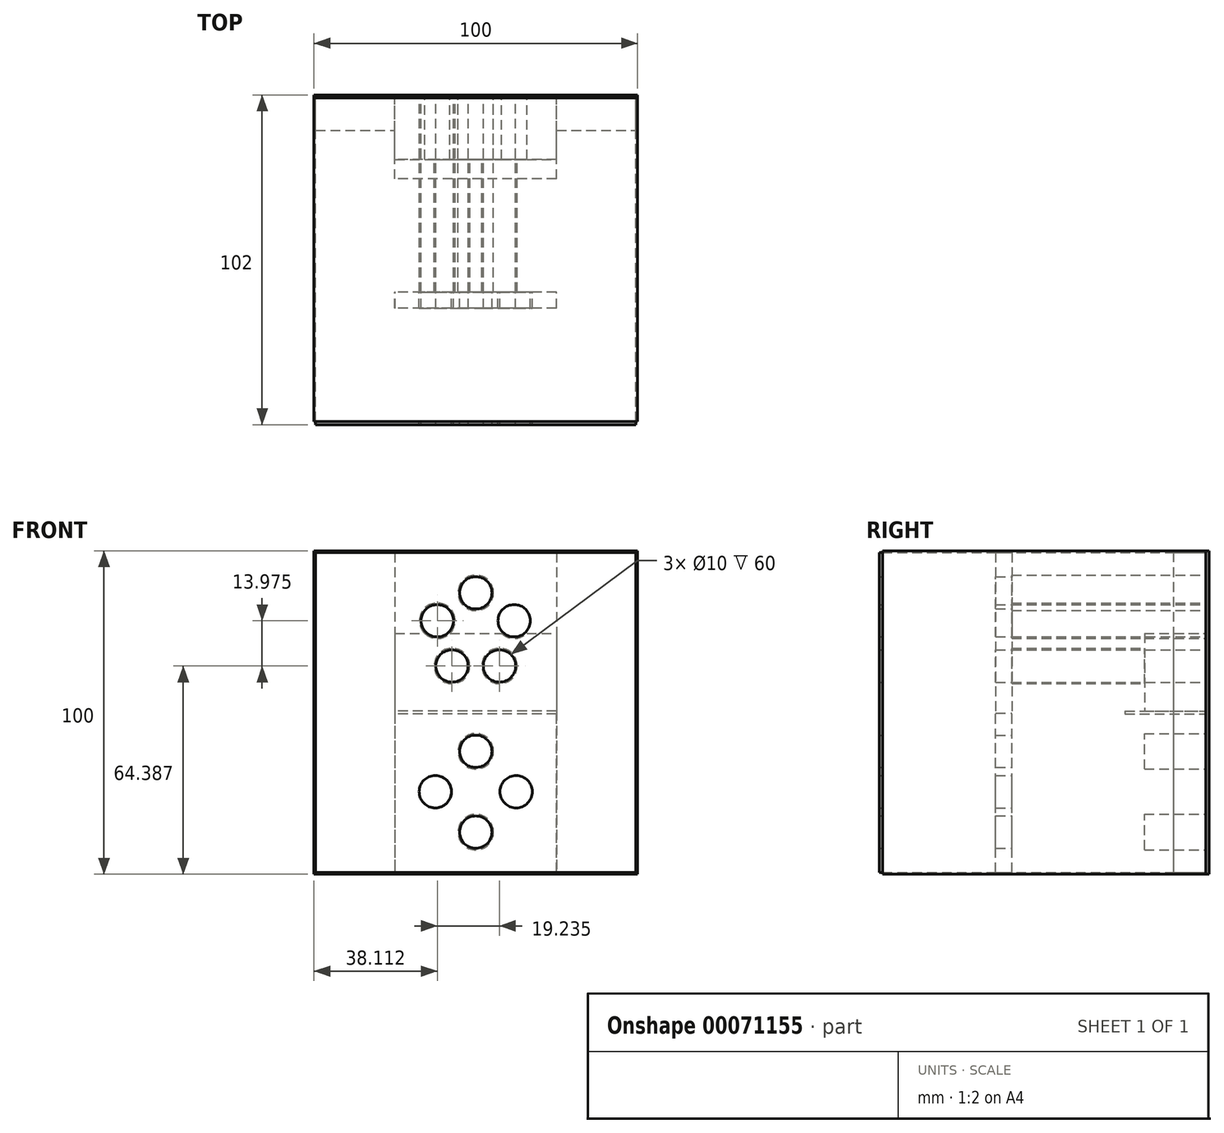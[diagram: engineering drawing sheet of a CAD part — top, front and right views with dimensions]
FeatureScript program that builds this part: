
annotation { "Feature Type Name" : "Feature", "Feature Type Description" : "" }
export const myFeature = defineFeature(function(context is Context, id is Id, definition is map)
    precondition{}
    {
        {
            var Q0;
            Q0=qCreatedBy(makeId("Front.planeOp"),FACE);
            var sketch = newSketch(context, id + "F0", { "sketchPlane" : qUnion([Q0])});
            skLineSegment(sketch, "E0.rect.bottom", {"start": v(-49.5, 49.5) * mm, "end": v(49.5, 49.5) * mm});
            skLineSegment(sketch, "E0.rect.top", {"start": v(-49.5, -49.5) * mm, "end": v(49.5, -49.5) * mm});
            skLineSegment(sketch, "E0.rect.left", {"start": v(-49.5, 49.5) * mm, "end": v(-49.5, -49.5) * mm});
            skLineSegment(sketch, "E0.rect.right", {"start": v(49.5, 49.5) * mm, "end": v(49.5, -49.5) * mm});
            skPoint(sketch, "E0.rect.middle", {"position": v(0, 0) * mm});
            skLineSegment(sketch, "E1", {"start": v(-49.5, 0) * mm, "end": v(49.5, 0) * mm});
            skLineSegment(sketch, "E2", {"start": v(0, 49.5) * mm, "end": v(0, -49.5) * mm});
            skLineSegment(sketch, "E3", {"start": v(-49.5, 24.5) * mm, "end": v(49.5, 24.5) * mm});
            skPoint(sketch, "E4", {"position": v(0, 24.5) * mm});
            skPoint(sketch, "E5", {"position": v(0, 37) * mm});
            skPoint(sketch, "E6", {"position": v(0, 12) * mm});
            skCircle(sketch, "E7", {"center": v(0, 37) * mm, "radius": 5.5 * mm});
            skPoint(sketch, "E8.1.0", {"position": v(-11.89, 28.36) * mm});
            skPoint(sketch, "E8.2.0", {"position": v(-7.35, 14.39) * mm});
            skPoint(sketch, "E8.3.0", {"position": v(7.35, 14.39) * mm});
            skCircle(sketch, "E9", {"center": v(-11.89, 28.36) * mm, "radius": 5.5 * mm});
            skCircle(sketch, "E10", {"center": v(11.89, 28.36) * mm, "radius": 5.5 * mm});
            skCircle(sketch, "E11", {"center": v(-7.35, 14.39) * mm, "radius": 5.5 * mm});
            skLineSegment(sketch, "E12", {"start": v(-49.5, -24.5) * mm, "end": v(49.5, -24.5) * mm});
            skPoint(sketch, "E13", {"position": v(0, -24.5) * mm});
            skPoint(sketch, "E14", {"position": v(0, -37) * mm});
            skPoint(sketch, "E15", {"position": v(0, -12) * mm});
            skCircle(sketch, "E16", {"center": v(7.35, 14.39) * mm, "radius": 5.5 * mm});
            skPoint(sketch, "E17.1.0", {"position": v(12.5, -24.5) * mm});
            skPoint(sketch, "E17.1.1", {"position": v(-24.5, -24.5) * mm});
            skLineSegment(sketch, "E17.1.2", {"start": v(-74, -24.5) * mm, "end": v(25, -24.5) * mm});
            skPoint(sketch, "E17.1.3", {"position": v(-12.5, -24.5) * mm});
            skPoint(sketch, "E17.2.1", {"position": v(0, -49) * mm});
            skLineSegment(sketch, "E17.2.2", {"start": v(0, -98.5) * mm, "end": v(0, 0.5) * mm});
            skPoint(sketch, "E17.3.0", {"position": v(-12.5, -24.5) * mm});
            skPoint(sketch, "E17.3.1", {"position": v(24.5, -24.5) * mm});
            skLineSegment(sketch, "E17.3.2", {"start": v(74, -24.5) * mm, "end": v(-25, -24.5) * mm});
            skPoint(sketch, "E17.3.3", {"position": v(12.5, -24.5) * mm});
            skCircle(sketch, "E18", {"center": v(-12.5, -24.5) * mm, "radius": 5.5 * mm});
            skCircle(sketch, "E19", {"center": v(0, -12) * mm, "radius": 5.5 * mm});
            skCircle(sketch, "E20", {"center": v(12.5, -24.5) * mm, "radius": 5.5 * mm});
            skCircle(sketch, "E21", {"center": v(0, -37) * mm, "radius": 5.5 * mm});
            skLineSegment(sketch, "E22.rect.bottom", {"start": v(25, 49.5) * mm, "end": v(-25, 49.5) * mm});
            skLineSegment(sketch, "E22.rect.top", {"start": v(25, -0.5) * mm, "end": v(-25, -0.5) * mm});
            skLineSegment(sketch, "E22.rect.left", {"start": v(25, 49.5) * mm, "end": v(25, -0.5) * mm});
            skLineSegment(sketch, "E22.rect.right", {"start": v(-25, 49.5) * mm, "end": v(-25, -0.5) * mm});
            skLineSegment(sketch, "E23.rect.bottom", {"start": v(25, 0.5) * mm, "end": v(-25, 0.5) * mm});
            skLineSegment(sketch, "E23.rect.top", {"start": v(25, -49.5) * mm, "end": v(-25, -49.5) * mm});
            skLineSegment(sketch, "E23.rect.left", {"start": v(25, 0.5) * mm, "end": v(25, -49.5) * mm});
            skLineSegment(sketch, "E23.rect.right", {"start": v(-25, 0.5) * mm, "end": v(-25, -49.5) * mm});
            skSolve(sketch);
        }
        {
            var Q0;
            Q0=makeQuery(id+"F0.imprint","IMPRINT",FACE,{"disambiguationData":[TD([[makeQuery(id+"F0.imprint","IMPRINT",EDGE,{"derivedFrom":sQuery(id+"F0.wireOp",EDGE,"E11")}),-1.0]])]});
            var Q1;
            {var subQ1=sQuery(id+"F0.wireOp",EDGE,"E2");var subQ8=sQuery(id+"F0.wireOp",EDGE,"E22.rect.bottom");var subQ9=makeQuery(id+"F0.imprint","INTERSECT",VERTEX,{"derivedFrom":[subQ1,subQ8]});Q1=makeQuery(id+"F0.imprint","IMPRINT",FACE,{"disambiguationData":[TD([[makeQuery(id+"F0.imprint","IMPRINT",EDGE,{"disambiguationData":[TD([[subQ9,-1.0]])],"derivedFrom":subQ1}),-1.0]])]});}
            var Q2;
            {var subQ6=sQuery(id+"F0.wireOp",EDGE,"E2");var subQ10=sQuery(id+"F0.wireOp",EDGE,"E22.rect.bottom");var subQ11=makeQuery(id+"F0.imprint","INTERSECT",VERTEX,{"derivedFrom":[subQ6,subQ10]});Q2=makeQuery(id+"F0.imprint","IMPRINT",FACE,{"disambiguationData":[TD([[makeQuery(id+"F0.imprint","IMPRINT",EDGE,{"disambiguationData":[TD([[subQ11,-1.0]])],"derivedFrom":subQ6}),1.0]])]});}
            var Q3;
            Q3=makeQuery(id+"F0.imprint","IMPRINT",FACE,{"disambiguationData":[TD([[makeQuery(id+"F0.imprint","IMPRINT",EDGE,{"derivedFrom":sQuery(id+"F0.wireOp",EDGE,"E16")}),-1.0]])]});
            var Q4;
            {var subQ0=sQuery(id+"F0.wireOp",EDGE,"E17.3.2");var subQ1=sQuery(id+"F0.wireOp",EDGE,"E17.2.2");var subQ2=makeQuery(id+"F0.imprint","INTERSECT",VERTEX,{"derivedFrom":[subQ1,subQ0]});Q4=makeQuery(id+"F0.imprint","IMPRINT",FACE,{"disambiguationData":[TD([[makeQuery(id+"F0.imprint","IMPRINT",EDGE,{"disambiguationData":[TD([[subQ2,-1.0]])],"derivedFrom":subQ1}),-1.0]])]});}
            var Q5;
            {var subQ1=sQuery(id+"F0.wireOp",EDGE,"E17.3.2");var subQ6=sQuery(id+"F0.wireOp",EDGE,"E17.2.2");var subQ10=makeQuery(id+"F0.imprint","INTERSECT",VERTEX,{"derivedFrom":[subQ6,subQ1]});Q5=makeQuery(id+"F0.imprint","IMPRINT",FACE,{"disambiguationData":[TD([[makeQuery(id+"F0.imprint","IMPRINT",EDGE,{"disambiguationData":[TD([[subQ10,-1.0]])],"derivedFrom":subQ6}),1.0]])]});}
            var Q6;
            {var subQ6=sQuery(id+"F0.wireOp",EDGE,"E17.2.2");var subQ11=sQuery(id+"F0.wireOp",EDGE,"E23.rect.top");var subQ13=makeQuery(id+"F0.imprint","INTERSECT",VERTEX,{"derivedFrom":[subQ6,subQ11]});Q6=makeQuery(id+"F0.imprint","IMPRINT",FACE,{"disambiguationData":[TD([[makeQuery(id+"F0.imprint","IMPRINT",EDGE,{"disambiguationData":[TD([[subQ13,-1.0]])],"derivedFrom":subQ6}),1.0]])]});}
            var Q7;
            {var subQ1=sQuery(id+"F0.wireOp",EDGE,"E17.2.2");var subQ10=sQuery(id+"F0.wireOp",EDGE,"E23.rect.top");var subQ11=makeQuery(id+"F0.imprint","INTERSECT",VERTEX,{"derivedFrom":[subQ1,subQ10]});Q7=makeQuery(id+"F0.imprint","IMPRINT",FACE,{"disambiguationData":[TD([[makeQuery(id+"F0.imprint","IMPRINT",EDGE,{"disambiguationData":[TD([[subQ11,-1.0]])],"derivedFrom":subQ1}),-1.0]])]});}
            extrude(context, id + "F1", {"entities" : qUnion([Q0, Q1, Q2, Q3, Q4, Q5, Q6, Q7]), "depth" : 19 * mm});
        }
        {
            var Q0;
            {var subQ0=sQuery(id+"F0.wireOp",EDGE,"E0.rect.left");var subQ1=sQuery(id+"F0.wireOp",EDGE,"E0.rect.bottom");var subQ2=makeQuery(id+"F0.imprint","INTERSECT",VERTEX,{"derivedFrom":[subQ1,subQ0]});Q0=makeQuery(id+"F0.imprint","IMPRINT",FACE,{"disambiguationData":[TD([[makeQuery(id+"F0.imprint","IMPRINT",EDGE,{"disambiguationData":[TD([[subQ2,-1.0]])],"derivedFrom":subQ0}),1.0]])]});}
            var Q1;
            {var subQ0=sQuery(id+"F0.wireOp",EDGE,"E1");var subQ1=sQuery(id+"F0.wireOp",EDGE,"E0.rect.left");var subQ2=makeQuery(id+"F0.imprint","INTERSECT",VERTEX,{"derivedFrom":[subQ1,subQ0]});Q1=makeQuery(id+"F0.imprint","IMPRINT",FACE,{"disambiguationData":[TD([[makeQuery(id+"F0.imprint","IMPRINT",EDGE,{"disambiguationData":[TD([[subQ2,1.0]])],"derivedFrom":subQ1}),1.0]])]});}
            var Q2;
            {var subQ0=sQuery(id+"F0.wireOp",EDGE,"E1");var subQ1=sQuery(id+"F0.wireOp",EDGE,"E0.rect.left");var subQ2=makeQuery(id+"F0.imprint","INTERSECT",VERTEX,{"derivedFrom":[subQ1,subQ0]});Q2=makeQuery(id+"F0.imprint","IMPRINT",FACE,{"disambiguationData":[TD([[makeQuery(id+"F0.imprint","IMPRINT",EDGE,{"disambiguationData":[TD([[subQ2,-1.0]])],"derivedFrom":subQ1}),1.0]])]});}
            var Q3;
            {var subQ0=sQuery(id+"F0.wireOp",EDGE,"E0.rect.left");var subQ1=sQuery(id+"F0.wireOp",EDGE,"E0.rect.top");var subQ2=makeQuery(id+"F0.imprint","INTERSECT",VERTEX,{"derivedFrom":[subQ1,subQ0]});Q3=makeQuery(id+"F0.imprint","IMPRINT",FACE,{"disambiguationData":[TD([[makeQuery(id+"F0.imprint","IMPRINT",EDGE,{"disambiguationData":[TD([[subQ2,1.0]])],"derivedFrom":subQ0}),1.0]])]});}
            var Q4;
            {var subQ0=sQuery(id+"F0.wireOp",EDGE,"E0.rect.right");var subQ1=sQuery(id+"F0.wireOp",EDGE,"E0.rect.top");var subQ2=makeQuery(id+"F0.imprint","INTERSECT",VERTEX,{"derivedFrom":[subQ1,subQ0]});Q4=makeQuery(id+"F0.imprint","IMPRINT",FACE,{"disambiguationData":[TD([[makeQuery(id+"F0.imprint","IMPRINT",EDGE,{"disambiguationData":[TD([[subQ2,1.0]])],"derivedFrom":subQ0}),-1.0]])]});}
            var Q5;
            {var subQ0=sQuery(id+"F0.wireOp",EDGE,"E1");var subQ1=sQuery(id+"F0.wireOp",EDGE,"E0.rect.right");var subQ2=makeQuery(id+"F0.imprint","INTERSECT",VERTEX,{"derivedFrom":[subQ1,subQ0]});Q5=makeQuery(id+"F0.imprint","IMPRINT",FACE,{"disambiguationData":[TD([[makeQuery(id+"F0.imprint","IMPRINT",EDGE,{"disambiguationData":[TD([[subQ2,-1.0]])],"derivedFrom":subQ1}),-1.0]])]});}
            var Q6;
            {var subQ0=sQuery(id+"F0.wireOp",EDGE,"E1");var subQ1=sQuery(id+"F0.wireOp",EDGE,"E0.rect.right");var subQ2=makeQuery(id+"F0.imprint","INTERSECT",VERTEX,{"derivedFrom":[subQ1,subQ0]});Q6=makeQuery(id+"F0.imprint","IMPRINT",FACE,{"disambiguationData":[TD([[makeQuery(id+"F0.imprint","IMPRINT",EDGE,{"disambiguationData":[TD([[subQ2,1.0]])],"derivedFrom":subQ1}),-1.0]])]});}
            var Q7;
            {var subQ0=sQuery(id+"F0.wireOp",EDGE,"E0.rect.right");var subQ1=sQuery(id+"F0.wireOp",EDGE,"E0.rect.bottom");var subQ2=makeQuery(id+"F0.imprint","INTERSECT",VERTEX,{"derivedFrom":[subQ1,subQ0]});Q7=makeQuery(id+"F0.imprint","IMPRINT",FACE,{"disambiguationData":[TD([[makeQuery(id+"F0.imprint","IMPRINT",EDGE,{"disambiguationData":[TD([[subQ2,-1.0]])],"derivedFrom":subQ0}),-1.0]])]});}
            extrude(context, id + "F2", {"entities" : qUnion([Q0, Q1, Q2, Q3, Q4, Q5, Q6, Q7]), "operationType" : NewBodyOperationType.ADD, "depth" : 10 * mm});
        }
        {
            var Q0;
            {var subQ0=sQuery(id+"F0.wireOp",EDGE,"E9");var subQ1=sQuery(id+"F0.wireOp",EDGE,"E3");var subQ2=makeQuery(id+"F0.imprint","INTERSECT",VERTEX,{"disambiguationData":[OD(0.0)],"derivedFrom":[subQ1,subQ0]});Q0=makeQuery(id+"F0.imprint","IMPRINT",FACE,{"disambiguationData":[TD([[makeQuery(id+"F0.imprint","IMPRINT",EDGE,{"disambiguationData":[TD([[subQ2,-1.0]])],"derivedFrom":subQ1}),1.0]])]});}
            var Q1;
            {var subQ0=sQuery(id+"F0.wireOp",EDGE,"E9");var subQ1=sQuery(id+"F0.wireOp",EDGE,"E3");var subQ2=makeQuery(id+"F0.imprint","INTERSECT",VERTEX,{"disambiguationData":[OD(0.0)],"derivedFrom":[subQ1,subQ0]});Q1=makeQuery(id+"F0.imprint","IMPRINT",FACE,{"disambiguationData":[TD([[makeQuery(id+"F0.imprint","IMPRINT",EDGE,{"disambiguationData":[TD([[subQ2,-1.0]])],"derivedFrom":subQ1}),-1.0]])]});}
            var Q2;
            {var subQ0=sQuery(id+"F0.wireOp",EDGE,"E7");var subQ1=sQuery(id+"F0.wireOp",EDGE,"E2");var subQ2=makeQuery(id+"F0.imprint","INTERSECT",VERTEX,{"disambiguationData":[OD(0.0)],"derivedFrom":[subQ1,subQ0]});Q2=makeQuery(id+"F0.imprint","IMPRINT",FACE,{"disambiguationData":[TD([[makeQuery(id+"F0.imprint","IMPRINT",EDGE,{"disambiguationData":[TD([[subQ2,-1.0]])],"derivedFrom":subQ1}),1.0]])]});}
            var Q3;
            {var subQ0=sQuery(id+"F0.wireOp",EDGE,"E7");var subQ1=sQuery(id+"F0.wireOp",EDGE,"E2");var subQ2=makeQuery(id+"F0.imprint","INTERSECT",VERTEX,{"disambiguationData":[OD(0.0)],"derivedFrom":[subQ1,subQ0]});Q3=makeQuery(id+"F0.imprint","IMPRINT",FACE,{"disambiguationData":[TD([[makeQuery(id+"F0.imprint","IMPRINT",EDGE,{"disambiguationData":[TD([[subQ2,-1.0]])],"derivedFrom":subQ1}),-1.0]])]});}
            var Q4;
            Q4=makeQuery(id+"F0.imprint","IMPRINT",FACE,{"disambiguationData":[TD([[makeQuery(id+"F0.imprint","IMPRINT",EDGE,{"derivedFrom":sQuery(id+"F0.wireOp",EDGE,"E16")}),1.0]])]});
            var Q5;
            Q5=makeQuery(id+"F0.imprint","IMPRINT",FACE,{"disambiguationData":[TD([[makeQuery(id+"F0.imprint","IMPRINT",EDGE,{"derivedFrom":sQuery(id+"F0.wireOp",EDGE,"E11")}),1.0]])]});
            var Q6;
            {var subQ0=sQuery(id+"F0.wireOp",EDGE,"E19");var subQ1=sQuery(id+"F0.wireOp",EDGE,"E17.2.2");var subQ2=makeQuery(id+"F0.imprint","INTERSECT",VERTEX,{"disambiguationData":[OD(0.0)],"derivedFrom":[subQ1,subQ0]});Q6=makeQuery(id+"F0.imprint","IMPRINT",FACE,{"disambiguationData":[TD([[makeQuery(id+"F0.imprint","IMPRINT",EDGE,{"disambiguationData":[TD([[subQ2,-1.0]])],"derivedFrom":subQ1}),-1.0]])]});}
            var Q7;
            {var subQ0=sQuery(id+"F0.wireOp",EDGE,"E19");var subQ1=sQuery(id+"F0.wireOp",EDGE,"E17.2.2");var subQ2=makeQuery(id+"F0.imprint","INTERSECT",VERTEX,{"disambiguationData":[OD(0.0)],"derivedFrom":[subQ1,subQ0]});Q7=makeQuery(id+"F0.imprint","IMPRINT",FACE,{"disambiguationData":[TD([[makeQuery(id+"F0.imprint","IMPRINT",EDGE,{"disambiguationData":[TD([[subQ2,-1.0]])],"derivedFrom":subQ1}),1.0]])]});}
            var Q8;
            {var subQ0=sQuery(id+"F0.wireOp",EDGE,"E18");var subQ1=sQuery(id+"F0.wireOp",EDGE,"E17.3.2");var subQ2=makeQuery(id+"F0.imprint","INTERSECT",VERTEX,{"disambiguationData":[OD(0.0)],"derivedFrom":[subQ1,subQ0]});Q8=makeQuery(id+"F0.imprint","IMPRINT",FACE,{"disambiguationData":[TD([[makeQuery(id+"F0.imprint","IMPRINT",EDGE,{"disambiguationData":[TD([[subQ2,-1.0]])],"derivedFrom":subQ1}),-1.0]])]});}
            var Q9;
            {var subQ0=sQuery(id+"F0.wireOp",EDGE,"E18");var subQ1=sQuery(id+"F0.wireOp",EDGE,"E17.3.2");var subQ2=makeQuery(id+"F0.imprint","INTERSECT",VERTEX,{"disambiguationData":[OD(0.0)],"derivedFrom":[subQ1,subQ0]});Q9=makeQuery(id+"F0.imprint","IMPRINT",FACE,{"disambiguationData":[TD([[makeQuery(id+"F0.imprint","IMPRINT",EDGE,{"disambiguationData":[TD([[subQ2,-1.0]])],"derivedFrom":subQ1}),1.0]])]});}
            var Q10;
            {var subQ0=sQuery(id+"F0.wireOp",EDGE,"E20");var subQ1=sQuery(id+"F0.wireOp",EDGE,"E17.3.2");var subQ2=makeQuery(id+"F0.imprint","INTERSECT",VERTEX,{"disambiguationData":[OD(0.0)],"derivedFrom":[subQ1,subQ0]});Q10=makeQuery(id+"F0.imprint","IMPRINT",FACE,{"disambiguationData":[TD([[makeQuery(id+"F0.imprint","IMPRINT",EDGE,{"disambiguationData":[TD([[subQ2,-1.0]])],"derivedFrom":subQ1}),-1.0]])]});}
            var Q11;
            {var subQ0=sQuery(id+"F0.wireOp",EDGE,"E20");var subQ1=sQuery(id+"F0.wireOp",EDGE,"E17.3.2");var subQ2=makeQuery(id+"F0.imprint","INTERSECT",VERTEX,{"disambiguationData":[OD(0.0)],"derivedFrom":[subQ1,subQ0]});Q11=makeQuery(id+"F0.imprint","IMPRINT",FACE,{"disambiguationData":[TD([[makeQuery(id+"F0.imprint","IMPRINT",EDGE,{"disambiguationData":[TD([[subQ2,-1.0]])],"derivedFrom":subQ1}),1.0]])]});}
            var Q12;
            {var subQ0=sQuery(id+"F0.wireOp",EDGE,"E21");var subQ1=sQuery(id+"F0.wireOp",EDGE,"E17.2.2");var subQ2=makeQuery(id+"F0.imprint","INTERSECT",VERTEX,{"disambiguationData":[OD(0.0)],"derivedFrom":[subQ1,subQ0]});Q12=makeQuery(id+"F0.imprint","IMPRINT",FACE,{"disambiguationData":[TD([[makeQuery(id+"F0.imprint","IMPRINT",EDGE,{"disambiguationData":[TD([[subQ2,-1.0]])],"derivedFrom":subQ1}),-1.0]])]});}
            var Q13;
            {var subQ0=sQuery(id+"F0.wireOp",EDGE,"E21");var subQ1=sQuery(id+"F0.wireOp",EDGE,"E17.2.2");var subQ2=makeQuery(id+"F0.imprint","INTERSECT",VERTEX,{"disambiguationData":[OD(0.0)],"derivedFrom":[subQ1,subQ0]});Q13=makeQuery(id+"F0.imprint","IMPRINT",FACE,{"disambiguationData":[TD([[makeQuery(id+"F0.imprint","IMPRINT",EDGE,{"disambiguationData":[TD([[subQ2,-1.0]])],"derivedFrom":subQ1}),1.0]])]});}
            var Q14;
            {var subQ0=sQuery(id+"F0.wireOp",EDGE,"da757bd1-b4bc-44ba-8823-31735c9c6de2");var subQ1=sQuery(id+"F0.wireOp",EDGE,"E3");var subQ2=makeQuery(id+"F0.imprint","INTERSECT",VERTEX,{"disambiguationData":[OD(0.0)],"derivedFrom":[subQ1,subQ0]});Q14=makeQuery(id+"F0.imprint","IMPRINT",FACE,{"disambiguationData":[TD([[makeQuery(id+"F0.imprint","IMPRINT",EDGE,{"disambiguationData":[TD([[subQ2,-1.0]])],"derivedFrom":subQ1}),-1.0]])]});}
            var Q15;
            {var subQ0=sQuery(id+"F0.wireOp",EDGE,"da757bd1-b4bc-44ba-8823-31735c9c6de2");var subQ1=sQuery(id+"F0.wireOp",EDGE,"E3");var subQ2=makeQuery(id+"F0.imprint","INTERSECT",VERTEX,{"disambiguationData":[OD(0.0)],"derivedFrom":[subQ1,subQ0]});Q15=makeQuery(id+"F0.imprint","IMPRINT",FACE,{"disambiguationData":[TD([[makeQuery(id+"F0.imprint","IMPRINT",EDGE,{"disambiguationData":[TD([[subQ2,-1.0]])],"derivedFrom":subQ1}),1.0]])]});}
            extrude(context, id + "F3", {"entities" : qUnion([Q0, Q1, Q2, Q3, Q4, Q5, Q6, Q7, Q8, Q9, Q10, Q11, Q12, Q13, Q14, Q15]), "operationType" : NewBodyOperationType.ADD, "depth" : 60 * mm});
        }
        {
            var Q0;
            {var subQ0=sQuery(id+"F0.wireOp",EDGE,"E23.rect.right");var subQ1=sQuery(id+"F0.wireOp",EDGE,"E1");var subQ2=makeQuery(id+"F0.imprint","INTERSECT",VERTEX,{"derivedFrom":[subQ1,subQ0]});Q0=makeQuery(id+"F0.imprint","IMPRINT",FACE,{"disambiguationData":[TD([[makeQuery(id+"F0.imprint","IMPRINT",EDGE,{"disambiguationData":[TD([[subQ2,-1.0]])],"derivedFrom":subQ1}),-1.0]])]});}
            var Q1;
            {var subQ0=sQuery(id+"F0.wireOp",EDGE,"E23.rect.right");var subQ1=sQuery(id+"F0.wireOp",EDGE,"E1");var subQ2=makeQuery(id+"F0.imprint","INTERSECT",VERTEX,{"derivedFrom":[subQ1,subQ0]});Q1=makeQuery(id+"F0.imprint","IMPRINT",FACE,{"disambiguationData":[TD([[makeQuery(id+"F0.imprint","IMPRINT",EDGE,{"disambiguationData":[TD([[subQ2,-1.0]])],"derivedFrom":subQ1}),1.0]])]});}
            var Q2;
            {var subQ0=sQuery(id+"F0.wireOp",EDGE,"E17.2.2");var subQ1=sQuery(id+"F0.wireOp",EDGE,"E1");var subQ2=makeQuery(id+"F0.imprint","INTERSECT",VERTEX,{"derivedFrom":[subQ1,subQ0]});Q2=makeQuery(id+"F0.imprint","IMPRINT",FACE,{"disambiguationData":[TD([[makeQuery(id+"F0.imprint","IMPRINT",EDGE,{"disambiguationData":[TD([[subQ2,-1.0]])],"derivedFrom":subQ1}),1.0]])]});}
            var Q3;
            {var subQ0=sQuery(id+"F0.wireOp",EDGE,"E17.2.2");var subQ1=sQuery(id+"F0.wireOp",EDGE,"E1");var subQ2=makeQuery(id+"F0.imprint","INTERSECT",VERTEX,{"derivedFrom":[subQ1,subQ0]});Q3=makeQuery(id+"F0.imprint","IMPRINT",FACE,{"disambiguationData":[TD([[makeQuery(id+"F0.imprint","IMPRINT",EDGE,{"disambiguationData":[TD([[subQ2,-1.0]])],"derivedFrom":subQ1}),-1.0]])]});}
            extrude(context, id + "F4", {"entities" : qUnion([Q0, Q1, Q2, Q3]), "depth" : 25 * mm});
        }
        {
            var Q0;
            Q0=sQuery(id+"F0.wireOp",VERTEX,"E8.1.0");
            var Q1;
            Q1=sQuery(id+"F0.wireOp",VERTEX,"E5");
            var Q2;
            Q2=sQuery(id+"F0.wireOp",VERTEX,"E10.center");
            var Q3;
            Q3=sQuery(id+"F0.wireOp",VERTEX,"E8.3.0");
            var Q4;
            Q4=sQuery(id+"F0.wireOp",VERTEX,"E8.2.0");
            var Q5;
            Q5=sQuery(id+"F0.wireOp",VERTEX,"E15");
            var Q6;
            Q6=sQuery(id+"F0.wireOp",VERTEX,"E17.1.3");
            var Q7;
            Q7=sQuery(id+"F0.wireOp",VERTEX,"E14");
            var Q8;
            Q8=sQuery(id+"F0.wireOp",VERTEX,"E17.3.3");
            var Q9;
            Q9=makeQuery(id+"F1.opExtrude","SWEPT_BODY",BODY,{"disambiguationData":[OSD([sQuery(id+"F0.wireOp",EDGE,"E7"),sQuery(id+"F0.wireOp",EDGE,"E9"),sQuery(id+"F0.wireOp",EDGE,"E10"),sQuery(id+"F0.wireOp",EDGE,"E11"),sQuery(id+"F0.wireOp",EDGE,"E16"),sQuery(id+"F0.wireOp",EDGE,"E22.rect.bottom"),sQuery(id+"F0.wireOp",EDGE,"E22.rect.left"),sQuery(id+"F0.wireOp",EDGE,"E22.rect.right"),sQuery(id+"F0.wireOp",EDGE,"E23.rect.bottom")])]});
            var Q10;
            Q10=makeQuery(id+"F3.opExtrude","SWEPT_BODY",BODY,{"disambiguationData":[OSD([sQuery(id+"F0.wireOp",EDGE,"da757bd1-b4bc-44ba-8823-31735c9c6de2")])]});
            var Q11;
            Q11=makeQuery(id+"F3.opExtrude","SWEPT_BODY",BODY,{"disambiguationData":[OSD([sQuery(id+"F0.wireOp",EDGE,"E19")])]});
            var Q12;
            Q12=makeQuery(id+"F3.opExtrude","SWEPT_BODY",BODY,{"disambiguationData":[OSD([sQuery(id+"F0.wireOp",EDGE,"E18")])]});
            var Q13;
            Q13=makeQuery(id+"F3.opExtrude","SWEPT_BODY",BODY,{"disambiguationData":[OSD([sQuery(id+"F0.wireOp",EDGE,"E21")])]});
            var Q14;
            Q14=makeQuery(id+"F3.opExtrude","SWEPT_BODY",BODY,{"disambiguationData":[OSD([sQuery(id+"F0.wireOp",EDGE,"E20")])]});
            hole(context, id + "F5", {"style" : HoleStyle.SIMPLE, "holeDiameter" : 10 * mm, "endStyle" : HoleEndStyle.THROUGH, "oppositeDirection" : true, "locations" : qUnion([Q0, Q1, Q2, Q3, Q4, Q5, Q6, Q7, Q8]), "scope" : qUnion([Q9, Q10, Q11, Q12, Q13, Q14])});
        }
        {
            var Q0;
            Q0=qCreatedBy(makeId("Front.planeOp"),FACE);
            var sketch = newSketch(context, id + "F6", { "sketchPlane" : qUnion([Q0])});
            skLineSegment(sketch, "E24.rect.bottom", {"start": v(50, 50) * mm, "end": v(-50, 50) * mm});
            skLineSegment(sketch, "E24.rect.top", {"start": v(50, -50) * mm, "end": v(-50, -50) * mm});
            skLineSegment(sketch, "E24.rect.left", {"start": v(50, 50) * mm, "end": v(50, -50) * mm});
            skLineSegment(sketch, "E24.rect.right", {"start": v(-50, 50) * mm, "end": v(-50, -50) * mm});
            skPoint(sketch, "E24.rect.middle", {"position": v(0, 0) * mm});
            skLineSegment(sketch, "E25.rect.bottom", {"start": v(49.5, -49.5) * mm, "end": v(-49.5, -49.5) * mm});
            skLineSegment(sketch, "E25.rect.top", {"start": v(49.5, 49.5) * mm, "end": v(-49.5, 49.5) * mm});
            skLineSegment(sketch, "E25.rect.left", {"start": v(49.5, -49.5) * mm, "end": v(49.5, 49.5) * mm});
            skLineSegment(sketch, "E25.rect.right", {"start": v(-49.5, -49.5) * mm, "end": v(-49.5, 49.5) * mm});
            skSolve(sketch);
        }
        {
            var Q0;
            Q0 = qSketchRegion(id + "F6", true);
            extrude(context, id + "F7", {"entities" : qUnion([Q0]), "depth" : 100 * mm});
        }
        {
            var Q0;
            Q0=makeQuery(id+"F7.opExtrude","CAP_FACE",FACE,{"disambiguationData":[OSD([sQuery(id+"F6.wireOp",EDGE,"E24.rect.bottom"),sQuery(id+"F6.wireOp",EDGE,"E24.rect.top"),sQuery(id+"F6.wireOp",EDGE,"E24.rect.left"),sQuery(id+"F6.wireOp",EDGE,"E24.rect.right"),sQuery(id+"F6.wireOp",EDGE,"E25.rect.bottom"),sQuery(id+"F6.wireOp",EDGE,"E25.rect.top"),sQuery(id+"F6.wireOp",EDGE,"E25.rect.left"),sQuery(id+"F6.wireOp",EDGE,"E25.rect.right")])],"isStart":false});
            var sketch = newSketch(context, id + "F8", { "sketchPlane" : qUnion([Q0])});
            skLineSegment(sketch, "E26.rect.bottom", {"start": v(49.5, 49.5) * mm, "end": v(-49.5, 49.5) * mm});
            skLineSegment(sketch, "E26.rect.top", {"start": v(49.5, -49.5) * mm, "end": v(-49.5, -49.5) * mm});
            skLineSegment(sketch, "E26.rect.left", {"start": v(49.5, 49.5) * mm, "end": v(49.5, -49.5) * mm});
            skLineSegment(sketch, "E26.rect.right", {"start": v(-49.5, 49.5) * mm, "end": v(-49.5, -49.5) * mm});
            skPoint(sketch, "E26.rect.middle", {"position": v(0, 0) * mm});
            skCircle(sketch, "E27", {"center": v(-11.89, 28.36) * mm, "radius": 5 * mm});
            skCircle(sketch, "E28", {"center": v(0, 37) * mm, "radius": 5 * mm});
            skCircle(sketch, "E29", {"center": v(11.89, 28.36) * mm, "radius": 5 * mm});
            skCircle(sketch, "E30", {"center": v(7.35, 14.39) * mm, "radius": 5 * mm});
            skCircle(sketch, "E31", {"center": v(-7.35, 14.39) * mm, "radius": 5 * mm});
            skCircle(sketch, "E32", {"center": v(-12.5, -24.5) * mm, "radius": 5 * mm});
            skCircle(sketch, "E33", {"center": v(0, -12) * mm, "radius": 5 * mm});
            skCircle(sketch, "E34", {"center": v(12.5, -24.5) * mm, "radius": 5 * mm});
            skCircle(sketch, "E35", {"center": v(0, -37) * mm, "radius": 5 * mm});
            skSolve(sketch);
        }
        {
            var Q0;
            Q0 = qSketchRegion(id + "F8", true);
            extrude(context, id + "F9", {"entities" : qUnion([Q0]), "depth" : 1 * mm});
        }
        {
            var Q0;
            Q0=qCreatedBy(makeId("Front.planeOp"),FACE);
            var sketch = newSketch(context, id + "F10", { "sketchPlane" : qUnion([Q0])});
            skLineSegment(sketch, "E36.rect.bottom", {"start": v(-50, 50) * mm, "end": v(50, 50) * mm});
            skLineSegment(sketch, "E36.rect.top", {"start": v(-50, -50) * mm, "end": v(50, -50) * mm});
            skLineSegment(sketch, "E36.rect.left", {"start": v(-50, 50) * mm, "end": v(-50, -50) * mm});
            skLineSegment(sketch, "E36.rect.right", {"start": v(50, 50) * mm, "end": v(50, -50) * mm});
            skPoint(sketch, "E36.rect.middle", {"position": v(0, 0) * mm});
            skSolve(sketch);
        }
        {
            var Q0;
            Q0 = qSketchRegion(id + "F10", true);
            extrude(context, id + "F11", {"entities" : qUnion([Q0]), "oppositeDirection" : true, "depth" : 1 * mm});
        }
        {
            var Q0;
            Q0=qCreatedBy(makeId("Front.planeOp"),FACE);
            cPlane(context, id + "F12", {"entities" : qUnion([Q0]), "cplaneType" : CPlaneType.OFFSET, "offset" : 60 * mm, "width" : 150 * mm, "height" : 150 * mm});
        }
        {
            var Q0;
            Q0=qCreatedBy(id+"F12.planeOp",FACE);
            var sketch = newSketch(context, id + "F13", { "sketchPlane" : qUnion([Q0])});
            skLineSegment(sketch, "E37.rect.bottom", {"start": v(24.98, 49.47) * mm, "end": v(-24.98, 49.47) * mm});
            skLineSegment(sketch, "E37.rect.top", {"start": v(24.98, -0.2) * mm, "end": v(-24.98, -0.2) * mm});
            skLineSegment(sketch, "E37.rect.left", {"start": v(24.98, 49.47) * mm, "end": v(24.98, -0.2) * mm});
            skLineSegment(sketch, "E37.rect.right", {"start": v(-24.98, 49.47) * mm, "end": v(-24.98, -0.2) * mm});
            skPoint(sketch, "E37.rect.middle", {"position": v(0, 24.63) * mm});
            skLineSegment(sketch, "E38.rect.bottom", {"start": v(24.96, -49.47) * mm, "end": v(-24.96, -49.47) * mm});
            skLineSegment(sketch, "E38.rect.top", {"start": v(24.96, 0.69) * mm, "end": v(-24.96, 0.69) * mm});
            skLineSegment(sketch, "E38.rect.left", {"start": v(24.96, -49.47) * mm, "end": v(24.96, 0.69) * mm});
            skLineSegment(sketch, "E38.rect.right", {"start": v(-24.96, -49.47) * mm, "end": v(-24.96, 0.69) * mm});
            skPoint(sketch, "E38.rect.middle", {"position": v(0, -24.4) * mm});
            skCircle(sketch, "E39", {"center": v(-12.5, -24.5) * mm, "radius": 5 * mm});
            skCircle(sketch, "E40", {"center": v(0, -12) * mm, "radius": 5 * mm});
            skCircle(sketch, "E41", {"center": v(12.5, -24.5) * mm, "radius": 5 * mm});
            skCircle(sketch, "E42", {"center": v(0, -36.99) * mm, "radius": 5 * mm});
            skCircle(sketch, "E43", {"center": v(0, 37) * mm, "radius": 5 * mm});
            skCircle(sketch, "E44", {"center": v(11.89, 28.36) * mm, "radius": 5 * mm});
            skCircle(sketch, "E45", {"center": v(7.35, 14.39) * mm, "radius": 5 * mm});
            skCircle(sketch, "E46", {"center": v(-7.35, 14.39) * mm, "radius": 5 * mm});
            skCircle(sketch, "E47", {"center": v(-11.89, 28.36) * mm, "radius": 5 * mm});
            skSolve(sketch);
        }
        {
            var Q0;
            Q0 = qSketchRegion(id + "F13", true);
            extrude(context, id + "F14", {"entities" : qUnion([Q0]), "depth" : 5 * mm});
        }
    });
